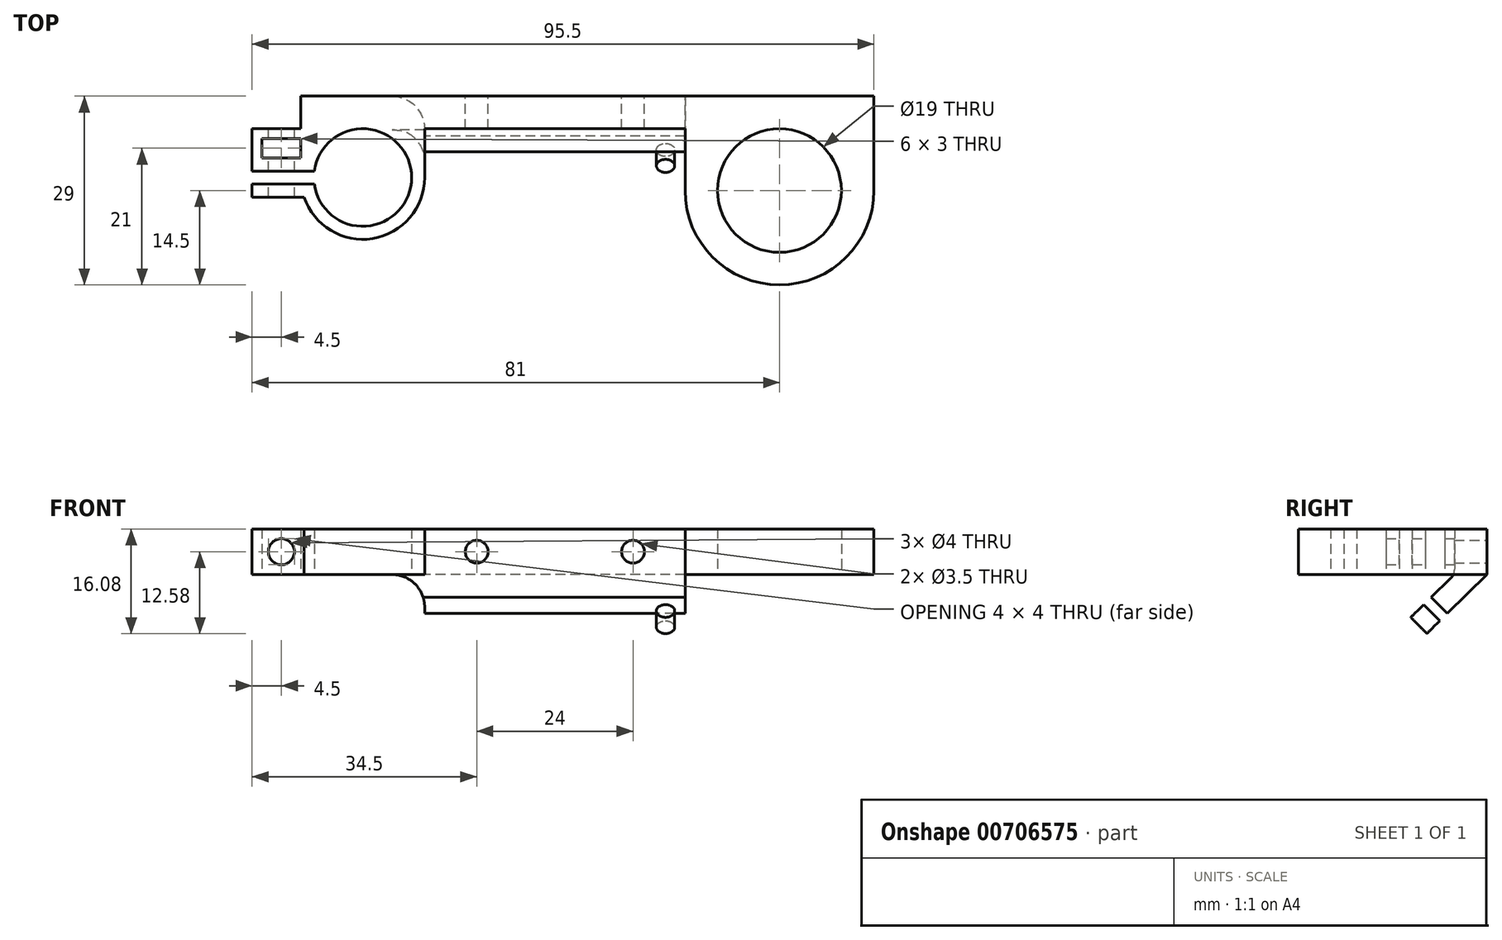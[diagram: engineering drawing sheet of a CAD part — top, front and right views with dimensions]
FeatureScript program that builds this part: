
annotation { "Feature Type Name" : "Feature", "Feature Type Description" : "" }
export const myFeature = defineFeature(function(context is Context, id is Id, definition is map)
    precondition{}
    {
        {
            var Q0;
            Q0=qCreatedBy(makeId("Front.planeOp"),FACE);
            var sketch = newSketch(context, id + "F0", { "sketchPlane" : qUnion([Q0])});
            skLineSegment(sketch, "E0.bottom", {"start": v(-32, 3.5) * mm, "end": v(42, 3.5) * mm});
            skLineSegment(sketch, "E0.top", {"start": v(-32, -3.5) * mm, "end": v(42, -3.5) * mm});
            skLineSegment(sketch, "E0.left", {"start": v(-32, 3.5) * mm, "end": v(-32, -3.5) * mm, "construction": true});
            skLineSegment(sketch, "E0.right", {"start": v(42, 3.5) * mm, "end": v(42, -3.5) * mm, "construction": true});
            skCircle(sketch, "E1", {"center": v(-12, 0) * mm, "radius": 1.75 * mm});
            skCircle(sketch, "E2", {"center": v(12, 0) * mm, "radius": 1.75 * mm});
            skLineSegment(sketch, "E3", {"start": v(-32, 3.5) * mm, "end": v(-39, 3.5) * mm});
            skLineSegment(sketch, "E4", {"start": v(-39, 3.5) * mm, "end": v(-39, -3.5) * mm});
            skLineSegment(sketch, "E5", {"start": v(-39, -3.5) * mm, "end": v(-32, -3.5) * mm});
            skLineSegment(sketch, "E6", {"start": v(42, 3.5) * mm, "end": v(49, 3.5) * mm});
            skLineSegment(sketch, "E7", {"start": v(49, 3.5) * mm, "end": v(49, -3.5) * mm});
            skLineSegment(sketch, "E8", {"start": v(49, -3.5) * mm, "end": v(42, -3.5) * mm});
            skLineSegment(sketch, "E9", {"start": v(0, 3.5) * mm, "end": v(0, 0) * mm, "construction": true});
            skLineSegment(sketch, "E10", {"start": v(0, 0) * mm, "end": v(0, -3.5) * mm, "construction": true});
            skLineSegment(sketch, "E11", {"start": v(-12, 0) * mm, "end": v(0, 0) * mm, "construction": true});
            skLineSegment(sketch, "E12", {"start": v(12, 0) * mm, "end": v(0, 0) * mm, "construction": true});
            skSolve(sketch);
        }
        {
            var Q0;
            Q0=makeQuery(id+"F0.imprint","IMPRINT",FACE,{"disambiguationData":[TD([[makeQuery(id+"F0.imprint","IMPRINT",EDGE,{"derivedFrom":sQuery(id+"F0.wireOp",EDGE,"E0.bottom")}),-1.0]])]});
            extrude(context, id + "F1", {"entities" : qUnion([Q0]), "depth" : 5 * mm, "offsetDistance" : 25 * mm});
        }
        {
            var Q0;
            Q0=qCreatedBy(makeId("Right.planeOp"),FACE);
            var sketch = newSketch(context, id + "F2", { "sketchPlane" : qUnion([Q0])});
            skLineSegment(sketch, "E13", {"start": v(-5, 0) * mm, "end": v(-5, -35) * mm, "construction": true});
            skLineSegment(sketch, "E14", {"start": v(-5, -3.5) * mm, "end": v(-37.14, -35) * mm});
            skLineSegment(sketch, "E15", {"start": v(-5, -35) * mm, "end": v(-37.14, -35) * mm, "construction": true});
            skLineSegment(sketch, "E16", {"start": v(-5, -3.5) * mm, "end": v(0, -3.5) * mm});
            skLineSegment(sketch, "E17", {"start": v(0, -3.5) * mm, "end": v(-32.14, -35) * mm});
            skLineSegment(sketch, "E18", {"start": v(-32.14, -35) * mm, "end": v(-37.14, -35) * mm});
            skLineSegment(sketch, "E19", {"start": v(-34.59, -32.5) * mm, "end": v(-32.14, -35) * mm});
            skSolve(sketch);
        }
        {
            var Q0;
            {var subQ1=sQuery(id+"F2.wireOp",EDGE,"E16");Q0=makeQuery(id+"F2.imprint","IMPRINT",FACE,{"disambiguationData":[TD([[makeQuery(id+"F2.imprint","IMPRINT",EDGE,{"derivedFrom":subQ1}),-1.0]])]});}
            extrude(context, id + "F3", {"entities" : qUnion([Q0]), "operationType" : NewBodyOperationType.ADD, "endBound" : BoundingType.SYMMETRIC, "depth" : 40 * mm, "offsetDistance" : 25 * mm});
        }
        {
            var Q0;
            Q0=makeQuery(id+"F3.opExtrude","SWEPT_FACE",FACE,{"disambiguationData":[OSD([sQuery(id+"F2.wireOp",EDGE,"E14")])]});
            var sketch = newSketch(context, id + "F4", { "sketchPlane" : qUnion([Q0])});
            skLineSegment(sketch, "E20", {"start": v(-20, -11.02) * mm, "end": v(20, -11.02) * mm, "construction": true});
            skLineSegment(sketch, "E21.bottom", {"start": v(-20, -11.02) * mm, "end": v(20, -11.02) * mm});
            skLineSegment(sketch, "E21.top", {"start": v(-20, -51.02) * mm, "end": v(20, -51.02) * mm});
            skLineSegment(sketch, "E21.left", {"start": v(-20, -11.02) * mm, "end": v(-20, -51.02) * mm});
            skLineSegment(sketch, "E21.right", {"start": v(20, -11.02) * mm, "end": v(20, -51.02) * mm});
            skLineSegment(sketch, "E22", {"start": v(-20, -11.02) * mm, "end": v(20, -51.02) * mm, "construction": true});
            skCircle(sketch, "E23", {"center": v(0, -31.02) * mm, "radius": 17 * mm});
            skCircle(sketch, "E24", {"center": v(-17, -14.02) * mm, "radius": 1.4 * mm});
            skCircle(sketch, "E25.MirrorC", {"center": v(17, -14.02) * mm, "radius": 1.4 * mm});
            skSolve(sketch);
        }
        {
            var Q0;
            {var subQ0=sQuery(id+"F4.wireOp",EDGE,"E23");var subQ1=makeQuery(id+"F3.opExtrude","SWEPT_EDGE",EDGE,{"disambiguationData":[OSD([sQuery(id+"F2.wireOp",EDGE,"E14"),sQuery(id+"F2.wireOp",EDGE,"LwI3nd4R-5eR8-zVZf-f6LJ-1cvqEujWtuRf")])]});var subQ2=makeQuery(id+"F4.imprint","INTERSECT",VERTEX,{"disambiguationData":[OD(0.0)],"derivedFrom":[subQ1,subQ0]});Q0=makeQuery(id+"F4.imprint","IMPRINT",FACE,{"disambiguationData":[TD([[makeQuery(id+"F4.imprint","IMPRINT",EDGE,{"disambiguationData":[TD([[subQ2,1.0]])],"derivedFrom":subQ0}),1.0]])]});}
            var Q1;
            {var subQ0=sQuery(id+"F4.wireOp",EDGE,"E23");var subQ1=makeQuery(id+"F3.opExtrude","SWEPT_EDGE",EDGE,{"disambiguationData":[OSD([sQuery(id+"F2.wireOp",EDGE,"E14"),sQuery(id+"F2.wireOp",EDGE,"LwI3nd4R-5eR8-zVZf-f6LJ-1cvqEujWtuRf")])]});var subQ2=makeQuery(id+"F4.imprint","INTERSECT",VERTEX,{"disambiguationData":[OD(0.0)],"derivedFrom":[subQ1,subQ0]});Q1=makeQuery(id+"F4.imprint","IMPRINT",FACE,{"disambiguationData":[TD([[makeQuery(id+"F4.imprint","IMPRINT",EDGE,{"disambiguationData":[TD([[subQ2,-1.0]])],"derivedFrom":subQ0}),1.0]])]});}
            var Q2;
            Q2=makeQuery(id+"F4.imprint","IMPRINT",FACE,{"disambiguationData":[TD([[makeQuery(id+"F4.imprint","IMPRINT",EDGE,{"derivedFrom":sQuery(id+"F4.wireOp",EDGE,"E24")}),1.0]])]});
            var Q3;
            Q3=makeQuery(id+"F4.imprint","IMPRINT",FACE,{"disambiguationData":[TD([[makeQuery(id+"F4.imprint","IMPRINT",EDGE,{"derivedFrom":sQuery(id+"F4.wireOp",EDGE,"E25.MirrorC")}),-1.0]])]});
            extrude(context, id + "F5", {"entities" : qUnion([Q0, Q1, Q2, Q3]), "operationType" : NewBodyOperationType.REMOVE, "endBound" : BoundingType.THROUGH_ALL, "oppositeDirection" : true, "depth" : 25 * mm, "offsetDistance" : 25 * mm});
        }
        {
            var Q0;
            {var subQ2=sQuery(id+"F11.wireOp",EDGE,"E47.top");var subQ3=sQuery(id+"F0.wireOp",EDGE,"E4");var subQ5=sQuery(id+"F0.wireOp",EDGE,"E8");var subQ8=sQuery(id+"F0.wireOp",EDGE,"E5");var subQ12=sQuery(id+"F0.wireOp",EDGE,"E0.top");Q0=makeQuery(id+"F3.boolean.opBoolean","SPLIT",FACE,{"disambiguationData":[TD([makeQuery(id+"F1.opExtrude","SWEPT_FACE",FACE,{"disambiguationData":[OSD([subQ3])]})])],"derivedFrom":makeQuery(id+"FjPR9svTBXWh2yE_1.boolean.opBoolean","MERGE",FACE,{"derivedFrom":[makeQuery(id+"F1.opExtrude","SWEPT_FACE",FACE,{"disambiguationData":[OSD([subQ12,subQ8,subQ5])]}),makeQuery(id+"FjPR9svTBXWh2yE_1.opExtrude","SWEPT_FACE",FACE,{"disambiguationData":[OSD([sQuery(id+"F11.wireOp",EDGE,"E46.top")])]}),makeQuery(id+"FjPR9svTBXWh2yE_1.opExtrude","SWEPT_FACE",FACE,{"disambiguationData":[OSD([subQ2])]})]})});}
            var sketch = newSketch(context, id + "F6", { "sketchPlane" : qUnion([Q0])});
            skCircle(sketch, "E26", {"center": v(-29.5, 12.5) * mm, "radius": 7.5 * mm});
            skCircle(sketch, "E27", {"center": v(-29.5, 12.5) * mm, "radius": 9.5 * mm});
            skLineSegment(sketch, "E28", {"start": v(-29.5, 12.5) * mm, "end": v(-46.5, 12.5) * mm, "construction": true});
            skLineSegment(sketch, "E29.bottom", {"start": v(-36.93, 13.5) * mm, "end": v(-46.5, 13.5) * mm});
            skLineSegment(sketch, "E29.top", {"start": v(-36.93, 11.5) * mm, "end": v(-46.5, 11.5) * mm});
            skLineSegment(sketch, "E29.left", {"start": v(-36.93, 13.5) * mm, "end": v(-36.93, 11.5) * mm, "construction": true});
            skLineSegment(sketch, "E29.right", {"start": v(-46.5, 13.5) * mm, "end": v(-46.5, 11.5) * mm, "construction": true});
            skPoint(sketch, "E29.middle", {"position": v(-41.72, 12.5) * mm});
            skLineSegment(sketch, "E30", {"start": v(-45, 11.5) * mm, "end": v(-45, 9.5) * mm, "construction": true});
            skLineSegment(sketch, "E31", {"start": v(-45, 9.5) * mm, "end": v(-46.5, 9.5) * mm, "construction": true});
            skLineSegment(sketch, "E32.bottom", {"start": v(-45, 9.5) * mm, "end": v(-39, 9.5) * mm});
            skLineSegment(sketch, "E32.top", {"start": v(-45, 6.5) * mm, "end": v(-39, 6.5) * mm});
            skLineSegment(sketch, "E32.left", {"start": v(-45, 9.5) * mm, "end": v(-45, 6.5) * mm});
            skLineSegment(sketch, "E32.right", {"start": v(-39, 9.5) * mm, "end": v(-39, 6.5) * mm});
            skLineSegment(sketch, "E33", {"start": v(-35.33, 5) * mm, "end": v(-46.5, 5) * mm});
            skLineSegment(sketch, "E34", {"start": v(-46.5, 11.5) * mm, "end": v(-46.5, 5) * mm});
            skLineSegment(sketch, "E35", {"start": v(-46.5, 13.5) * mm, "end": v(-46.5, 15.5) * mm});
            skLineSegment(sketch, "E36", {"start": v(-46.5, 15.5) * mm, "end": v(-38.51, 15.5) * mm});
            skLineSegment(sketch, "E37", {"start": v(-39, 6.5) * mm, "end": v(-39, 5) * mm, "construction": true});
            skLineSegment(sketch, "E38", {"start": v(-20, 5) * mm, "end": v(-20, 12.5) * mm});
            skCircle(sketch, "E39", {"center": v(34.5, 14.5) * mm, "radius": 9.5 * mm});
            skCircle(sketch, "E40", {"center": v(34.5, 14.5) * mm, "radius": 14.5 * mm});
            skLineSegment(sketch, "E41", {"start": v(20, 14.5) * mm, "end": v(20, 0) * mm});
            skLineSegment(sketch, "E42", {"start": v(20, 0) * mm, "end": v(49, 0) * mm});
            skLineSegment(sketch, "E43", {"start": v(49, 0) * mm, "end": v(49, 14.5) * mm});
            skSolve(sketch);
        }
        {
            var Q0;
            {var subQ0=sQuery(id+"F6.wireOp",EDGE,"E27");var subQ1=sQuery(id+"F0.wireOp",EDGE,"E8");var subQ2=sQuery(id+"F0.wireOp",EDGE,"E5");var subQ3=sQuery(id+"F0.wireOp",EDGE,"E0.top");var subQ4=sQuery(id+"F0.wireOp",EDGE,"E4");var subQ6=makeQuery(id+"F3.boolean.opBoolean","SPLIT",EDGE,{"disambiguationData":[TD([makeQuery(id+"F1.opExtrude","SWEPT_FACE",FACE,{"disambiguationData":[OSD([subQ4])]})])],"derivedFrom":makeQuery(id+"F1.opExtrude","CAP_EDGE",EDGE,{"disambiguationData":[OSD([subQ3,subQ2,subQ1])],"isStart":false})});var subQ8=makeQuery(id+"F6.imprint","INTERSECT",VERTEX,{"derivedFrom":[subQ6,subQ0]});Q0=makeQuery(id+"F6.imprint","IMPRINT",FACE,{"disambiguationData":[TD([[makeQuery(id+"F6.imprint","IMPRINT",EDGE,{"disambiguationData":[TD([[subQ8,1.0]])],"derivedFrom":subQ0}),1.0]])]});}
            var Q1;
            {var subQ0=sQuery(id+"F6.wireOp",EDGE,"E29.top");var subQ1=sQuery(id+"F6.wireOp",EDGE,"E26");var subQ2=makeQuery(id+"F6.imprint","INTERSECT",VERTEX,{"derivedFrom":[subQ1,subQ0]});Q1=makeQuery(id+"F6.imprint","IMPRINT",FACE,{"disambiguationData":[TD([[makeQuery(id+"F6.imprint","IMPRINT",EDGE,{"disambiguationData":[TD([[subQ2,-1.0]])],"derivedFrom":subQ0}),1.0]])]});}
            var Q2;
            {var subQ3=sQuery(id+"F6.wireOp",EDGE,"E27");var subQ5=makeQuery(id+"F6.imprint","INTERSECT",VERTEX,{"derivedFrom":[subQ3,sQuery(id+"F6.wireOp",EDGE,"E36")]});Q2=makeQuery(id+"F6.imprint","IMPRINT",FACE,{"disambiguationData":[TD([[makeQuery(id+"F6.imprint","IMPRINT",EDGE,{"disambiguationData":[TD([[subQ5,-1.0]])],"derivedFrom":subQ3}),1.0]])]});}
            var Q3;
            {var subQ4=sQuery(id+"F6.wireOp",EDGE,"E35");Q3=makeQuery(id+"F6.imprint","IMPRINT",FACE,{"disambiguationData":[TD([[makeQuery(id+"F6.imprint","IMPRINT",EDGE,{"derivedFrom":subQ4}),-1.0]])]});}
            var Q4;
            Q4=makeQuery(id+"F6.imprint","IMPRINT",FACE,{"disambiguationData":[TD([[makeQuery(id+"F6.imprint","IMPRINT",EDGE,{"derivedFrom":sQuery(id+"F6.wireOp",EDGE,"E32.bottom")}),1.0]])]});
            var Q5;
            {var subQ0=sQuery(id+"F6.wireOp",EDGE,"E38");Q5=makeQuery(id+"F6.imprint","IMPRINT",FACE,{"disambiguationData":[TD([[makeQuery(id+"F6.imprint","IMPRINT",EDGE,{"derivedFrom":subQ0}),1.0]])]});}
            var Q6;
            Q6=makeQuery(id+"FjPR9svTBXWh2yE_1.boolean.opBoolean","MERGE",FACE,{"derivedFrom":[makeQuery(id+"F1.opExtrude","SWEPT_FACE",FACE,{"disambiguationData":[OSD([sQuery(id+"F0.wireOp",EDGE,"E0.bottom"),sQuery(id+"F0.wireOp",EDGE,"E3"),sQuery(id+"F0.wireOp",EDGE,"E6")])]}),makeQuery(id+"FjPR9svTBXWh2yE_1.opExtrude","SWEPT_FACE",FACE,{"disambiguationData":[OSD([sQuery(id+"F11.wireOp",EDGE,"E46.bottom")])]}),makeQuery(id+"FjPR9svTBXWh2yE_1.opExtrude","SWEPT_FACE",FACE,{"disambiguationData":[OSD([sQuery(id+"F11.wireOp",EDGE,"E47.bottom")])]})]});
            extrude(context, id + "F7", {"entities" : qUnion([Q0, Q1, Q2, Q3, Q4, Q5]), "operationType" : NewBodyOperationType.ADD, "endBound" : BoundingType.UP_TO_SURFACE, "oppositeDirection" : true, "depth" : 25 * mm, "endBoundEntityFace" : qUnion([Q6]), "offsetDistance" : 25 * mm});
        }
        {
            var Q0;
            Q0=makeQuery(id+"F7.opExtrude","SWEPT_FACE",FACE,{"disambiguationData":[OSD([sQuery(id+"F6.wireOp",EDGE,"E32.top")])]});
            var sketch = newSketch(context, id + "F8", { "sketchPlane" : qUnion([Q0])});
            skLineSegment(sketch, "E44", {"start": v(-45, 3.5) * mm, "end": v(-39, -3.5) * mm, "construction": true});
            skCircle(sketch, "E45", {"center": v(-42, 0) * mm, "radius": 2 * mm});
            skSolve(sketch);
        }
        {
            var Q0;
            Q0=makeQuery(id+"F8.imprint","IMPRINT",FACE,{"disambiguationData":[TD([[makeQuery(id+"F8.imprint","IMPRINT",EDGE,{"derivedFrom":sQuery(id+"F8.wireOp",EDGE,"E45")}),1.0]])]});
            var Q1;
            Q1=makeQuery(id+"F7.opExtrude","SWEPT_FACE",FACE,{"disambiguationData":[OSD([sQuery(id+"F6.wireOp",EDGE,"E36")])]});
            var Q2;
            Q2=makeQuery(id+"F7.opExtrude","SWEPT_FACE",FACE,{"disambiguationData":[OSD([sQuery(id+"F6.wireOp",EDGE,"E33")])]});
            extrude(context, id + "F9", {"entities" : qUnion([Q0]), "operationType" : NewBodyOperationType.REMOVE, "endBound" : BoundingType.UP_TO_SURFACE, "depth" : 25 * mm, "endBoundEntityFace" : qUnion([Q1]), "offsetDistance" : 25 * mm, "hasSecondDirection" : true, "secondDirectionBound" : SecondDirectionBoundingType.UP_TO_SURFACE, "secondDirectionOppositeDirection" : true, "secondDirectionDepth" : 25 * mm, "secondDirectionBoundEntityFace" : qUnion([Q2])});
        }
        {
            var Q0;
            Q0=makeQuery(id+"F6.imprint","IMPRINT",FACE,{"disambiguationData":[TD([[makeQuery(id+"F6.imprint","IMPRINT",EDGE,{"derivedFrom":sQuery(id+"F6.wireOp",EDGE,"E39")}),-1.0]])]});
            var Q1;
            {var subQ0=sQuery(id+"F6.wireOp",EDGE,"E41");Q1=makeQuery(id+"F6.imprint","IMPRINT",FACE,{"disambiguationData":[TD([[makeQuery(id+"F6.imprint","IMPRINT",EDGE,{"derivedFrom":subQ0}),1.0]])]});}
            var Q2;
            {var subQ0=sQuery(id+"F6.wireOp",EDGE,"E43");Q2=makeQuery(id+"F6.imprint","IMPRINT",FACE,{"disambiguationData":[TD([[makeQuery(id+"F6.imprint","IMPRINT",EDGE,{"derivedFrom":subQ0}),1.0]])]});}
            var Q3;
            {var subQ0=sQuery(id+"F0.wireOp",EDGE,"E6");var subQ1=sQuery(id+"F0.wireOp",EDGE,"E3");var subQ2=sQuery(id+"F0.wireOp",EDGE,"E0.bottom");Q3=makeQuery(id+"F7.boolean.opBoolean","MERGE",FACE,{"derivedFrom":[makeQuery(id+"F1.opExtrude","SWEPT_FACE",FACE,{"disambiguationData":[OSD([subQ2,subQ1,subQ0])]}),makeQuery(id+"F7.opExtrude","CAP_FACE",FACE,{"disambiguationData":[OSD([subQ2,subQ1,subQ0])],"isStart":false})]});}
            extrude(context, id + "F10", {"entities" : qUnion([Q0, Q1, Q2]), "operationType" : NewBodyOperationType.ADD, "endBound" : BoundingType.UP_TO_SURFACE, "oppositeDirection" : true, "depth" : 25 * mm, "endBoundEntityFace" : qUnion([Q3]), "offsetDistance" : 25 * mm});
        }
        {
            var Q0;
            Q0=makeQuery(id+"F1.opExtrude","CAP_FACE",FACE,{"disambiguationData":[OSD([sQuery(id+"F0.wireOp",EDGE,"E0.bottom"),sQuery(id+"F0.wireOp",EDGE,"E0.top"),sQuery(id+"F0.wireOp",EDGE,"E1"),sQuery(id+"F0.wireOp",EDGE,"E2"),sQuery(id+"F0.wireOp",EDGE,"E3"),sQuery(id+"F0.wireOp",EDGE,"E4"),sQuery(id+"F0.wireOp",EDGE,"E5"),sQuery(id+"F0.wireOp",EDGE,"E6"),sQuery(id+"F0.wireOp",EDGE,"E7"),sQuery(id+"F0.wireOp",EDGE,"E8")])],"isStart":true});
            var sketch = newSketch(context, id + "F11", { "sketchPlane" : qUnion([Q0])});
            skLineSegment(sketch, "E46.bottom", {"start": v(-49, 3.5) * mm, "end": v(-44, 3.5) * mm});
            skLineSegment(sketch, "E46.top", {"start": v(-49, -3.5) * mm, "end": v(-44, -3.5) * mm});
            skLineSegment(sketch, "E46.left", {"start": v(-49, 3.5) * mm, "end": v(-49, -3.5) * mm});
            skLineSegment(sketch, "E46.right", {"start": v(-44, 3.5) * mm, "end": v(-44, -3.5) * mm});
            skLineSegment(sketch, "E47.bottom", {"start": v(39, 3.5) * mm, "end": v(34, 3.5) * mm});
            skLineSegment(sketch, "E47.top", {"start": v(39, -3.5) * mm, "end": v(34, -3.5) * mm});
            skLineSegment(sketch, "E47.left", {"start": v(39, 3.5) * mm, "end": v(39, -3.5) * mm});
            skLineSegment(sketch, "E47.right", {"start": v(34, 3.5) * mm, "end": v(34, -3.5) * mm});
            skSolve(sketch);
        }
        {
            var Q0;
            Q0=makeQuery(id+"F3.boolean.opBoolean","MERGE",EDGE,{"derivedFrom":[makeQuery(id+"F1.opExtrude","CAP_EDGE",EDGE,{"disambiguationData":[OSD([sQuery(id+"F0.wireOp",EDGE,"E0.top"),sQuery(id+"F0.wireOp",EDGE,"E5"),sQuery(id+"F0.wireOp",EDGE,"E8")])],"isStart":false}),makeQuery(id+"F3.opExtrude","SWEPT_EDGE",EDGE,{"disambiguationData":[OSD([sQuery(id+"F2.wireOp",EDGE,"E14"),sQuery(id+"F2.wireOp",EDGE,"E16")])]})]});
            fillet(context, id + "F12", {"entities" : qUnion([Q0]), "radius" : 2 * mm, "tangentPropagation" : true, "allowEdgeOverflow" : false});
        }
        {
            var Q0;
            Q0=makeQuery(id+"F3.opExtrude","CAP_EDGE",EDGE,{"disambiguationData":[OSD([sQuery(id+"F2.wireOp",EDGE,"E16")])],"isStart":true});
            var Q1;
            Q1=makeQuery(id+"F3.opExtrude","CAP_EDGE",EDGE,{"disambiguationData":[OSD([sQuery(id+"F2.wireOp",EDGE,"E16")])],"isStart":false});
            fillet(context, id + "F13", {"entities" : qUnion([Q0, Q1]), "radius" : 5 * mm, "tangentPropagation" : true, "allowEdgeOverflow" : false});
        }
    });
